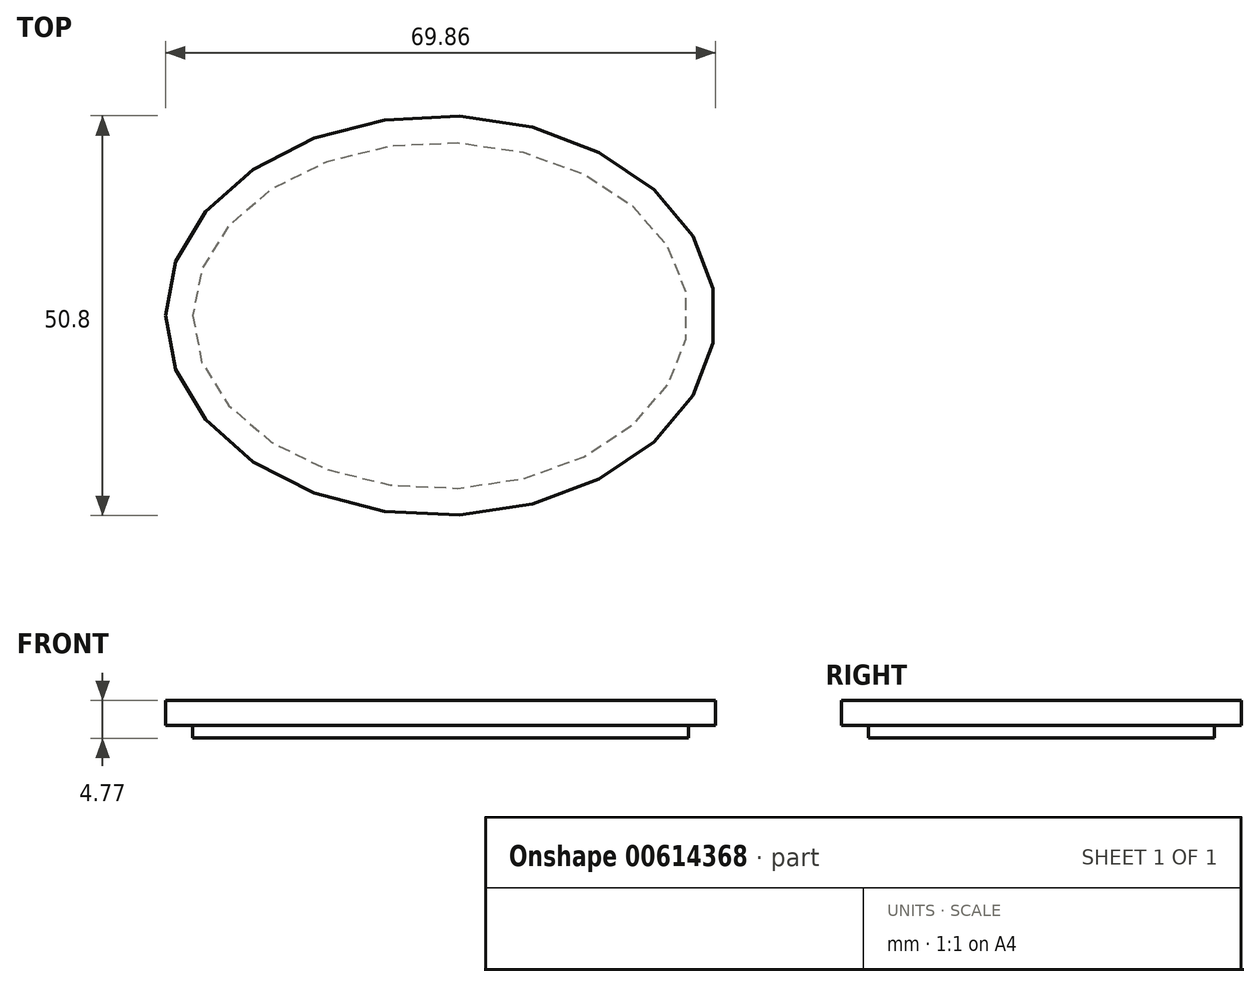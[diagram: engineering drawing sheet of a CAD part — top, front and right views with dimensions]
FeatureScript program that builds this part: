
annotation { "Feature Type Name" : "Feature", "Feature Type Description" : "" }
export const myFeature = defineFeature(function(context is Context, id is Id, definition is map)
    precondition{}
    {
        {
            var Q0;
            Q0=qCreatedBy(makeId("Top.planeOp"),FACE);
            var sketch = newSketch(context, id + "F0", { "sketchPlane" : qUnion([Q0])});
            skEllipse(sketch, "E0", {"center": v(0, 0) * mm, "majorRadius": 31.5 * mm, "minorRadius": 21.97 * mm, "majorAxis": v(-1, 0)});
            skPoint(sketch, "E1", {"position": v(0, 21.97) * mm});
            skPoint(sketch, "E2", {"position": v(-31.5, 0) * mm});
            skPoint(sketch, "E3", {"position": v(0, -21.97) * mm});
            skPoint(sketch, "E4", {"position": v(31.5, 0) * mm});
            skSolve(sketch);
        }
        {
            var Q0;
            Q0 = qSketchRegion(id + "F0", true);
            extrude(context, id + "F1", {"entities" : qUnion([Q0]), "flatOperationType" : FlatOperationType.REMOVE, "oppositeDirection" : true, "depth" : 1.59 * mm, "offsetDistance" : 25.4 * mm, "domain" : OperationDomain.MODEL});
        }
        {
            var Q0;
            Q0=makeQuery(id+"F1.opExtrude","CAP_FACE",FACE,{"disambiguationData":[OSD([sQuery(id+"F0.wireOp",EDGE,"E0")])],"isStart":true});
            var sketch = newSketch(context, id + "F2", { "sketchPlane" : qUnion([Q0])});
            skEllipse(sketch, "E5", {"center": v(0, 0) * mm, "majorRadius": 34.93 * mm, "minorRadius": 25.4 * mm, "majorAxis": v(-1, 0)});
            skSolve(sketch);
        }
        {
            var Q0;
            Q0 = qSketchRegion(id + "F2", true);
            extrude(context, id + "F3", {"entities" : qUnion([Q0]), "flatOperationType" : FlatOperationType.REMOVE, "depth" : 3.17 * mm, "offsetDistance" : 25.4 * mm, "domain" : OperationDomain.MODEL});
        }
    });
